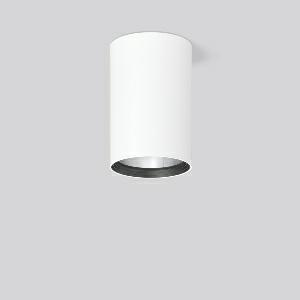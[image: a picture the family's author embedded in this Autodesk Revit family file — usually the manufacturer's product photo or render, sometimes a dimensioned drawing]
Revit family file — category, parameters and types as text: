
# Revit family: heledon_maxi_a_931225_002_1_76_f085
name_source: partatom
category: Lighting Fixtures
units: mm (PartAtom-declared; Revit-internal decimal feet)

## family parameters
Cut with Voids When Loaded = No
Host = Face
Light Source = No
Part Type = Normal
Room Calculation Point = No
Round Connector Dimension = Use Diameter
Shared = No

## types (1)
- HELEDON maxi A (1 x LED Modul 940, 4550 lm, 4000)
    Apparent Load = 35 VA
    Approval mark = CE
    CIE Flux Codes = 100 100 100 100 100
    Color Rendering = 92
    Color Temperature = 4000
    Default Elevation = 1800 mm
    Description = Series: HELEDON maxi
Cylindrical surface-mounted downlight. Housing: die-cast aluminium, powder-coated. Internal ceiling frame polycarbonate with bayonet mounting. Black plastic ring and recessed LED to prevent glare from the side. Optical assembly with reflector made of MIRO-Silver with 98% total light reflection for outstanding efficiency - can be changed without tools. Best colour rendering index Ra>90. Suitable for Ceiling mounting. Easy installation with a separate ceiling frame with bayonet mounting and plug connection. Driver integrated. Connected via plug-in connector. High quality converter without flickering and stroboscopic effect. The following accessories can be mounted without use of tools: interchangeable lenses, decorative glasses, honeycomb louvre, clear and frosted diffusers, white interchangeable plastic ring. 
Colour: traffic white, matt (RAL 9016)
Diameter: 123 mm
Height: 183 mm
Lamp: LED
Socket: without socket
Colour temperature: 4000K
Colour rendering index (CRI): 92
System power: 35 W
Rated luminous flux: 4550 lm
Luminous efficiency: 130 lm/W
Control gear: Converter, dimmable, DALI
Protection class: I
Type of protection: IP 20
    Height = 183 mm
    Lamp = 1 x LED Modul 940
    Lamp Light Flux = 4550 lm
    Lamp count = 1
    Length = 123 mm
    Lifetime = 50000 h
    Luminous efficacy = 130 lm/W
    Manufacturer = RZB
    ModVariant = No
    Model = 931225.002.1.76
    Mounting Place = Ceiling
    Mounting Type = Surface mounted
    Number of Poles = 1
    OnlyDefault = Yes
    Power Factor = 1
    Product Name = HELEDON maxi A
    Product group = Surface mounted downlights
    ProductGroupID = 302
    Protection Class = Protection class I
    Protection Degree = IP 20
    RLX_Detail_Level = 1
    RLX_Emergency_Light_Flux = 0 lm
    RLX_Emergency_Type = 0
    RLX_Emergency_Type_DB = No
    RlxData = <blob elided: 98657 chars, md5=a80a7b5d>
    Socket = socket
    Standby Power = 0 W
    System Light Flux = 4550 lm
    System Power = 35 W
    Type Comments = Product without accessories
    Type Image = 931192.002.jpg
    URL = http://relux.com
    VarID = ---
    Voltage = 230 V
    Voltage Range = 220-240 V
    Weight = 0.00 kg
    Width = 0 mm  [stored 0 ft]

note: [stored X ft] marks values corroborated as IEEE doubles in the binary element streams (Revit-internal decimal feet)

## geometry (parser evidence)
native form markers: Blend x4, Sweep x11
no freeform markers — native parametric forms only
